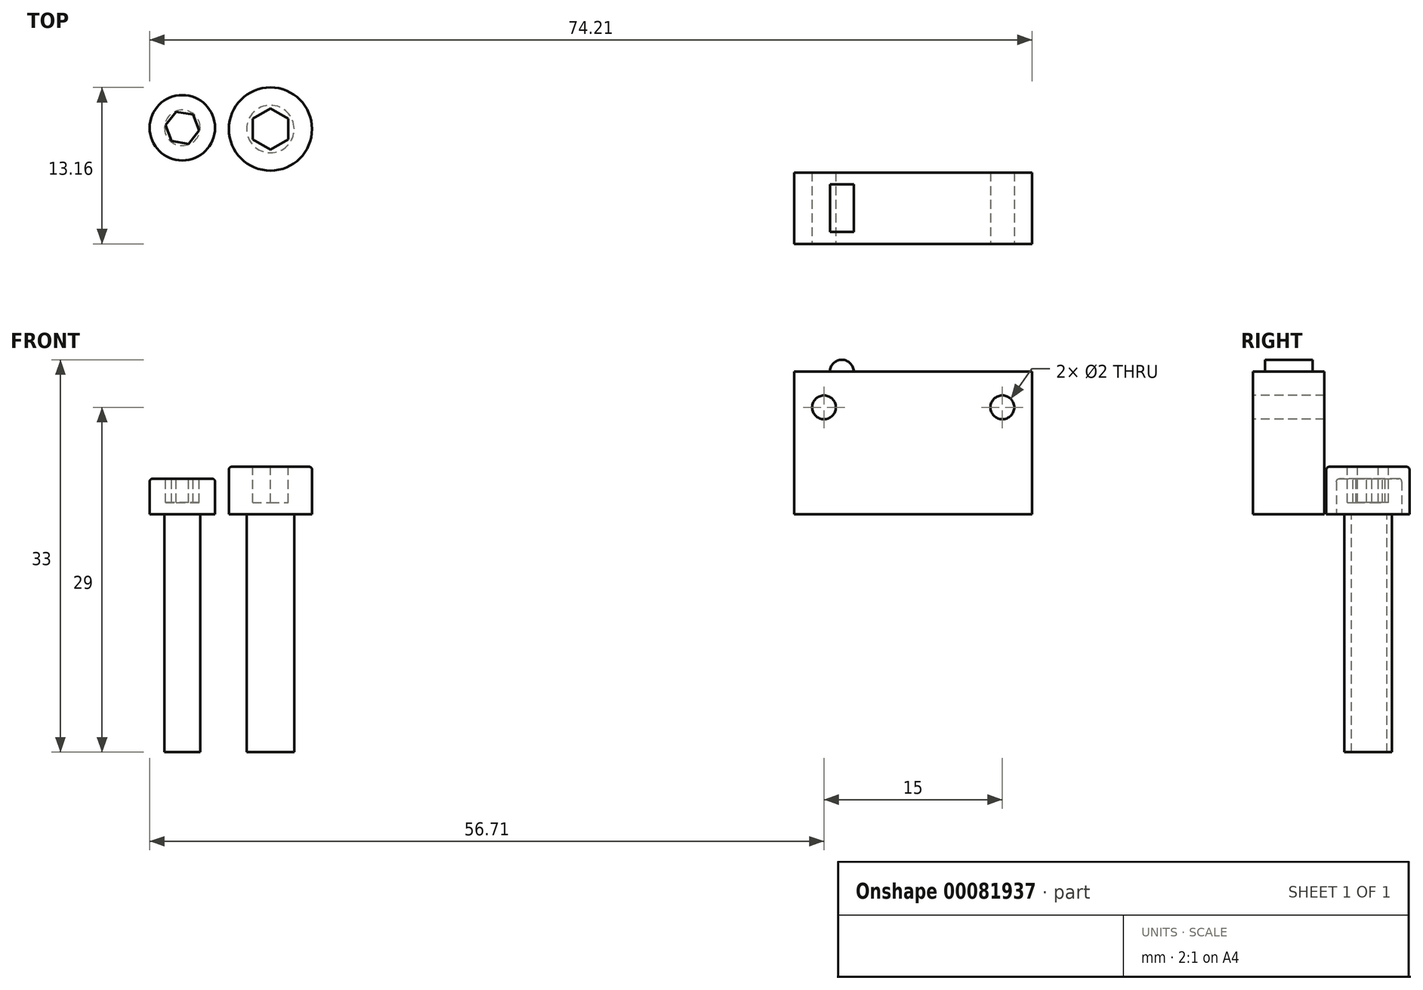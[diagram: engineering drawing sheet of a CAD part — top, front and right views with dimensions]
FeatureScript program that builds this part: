
annotation { "Feature Type Name" : "Feature", "Feature Type Description" : "" }
export const myFeature = defineFeature(function(context is Context, id is Id, definition is map)
    precondition{}
    {
        {
            var Q0;
            Q0=qCreatedBy(makeId("Front.planeOp"),FACE);
            var sketch = newSketch(context, id + "F0", { "sketchPlane" : qUnion([Q0])});
            skLineSegment(sketch, "E0.bottom", {"start": v(-10, 12) * mm, "end": v(10, 12) * mm});
            skLineSegment(sketch, "E0.top", {"start": v(-10, 0) * mm, "end": v(10, 0) * mm});
            skLineSegment(sketch, "E0.left", {"start": v(-10, 12) * mm, "end": v(-10, 0) * mm});
            skLineSegment(sketch, "E0.right", {"start": v(10, 12) * mm, "end": v(10, 0) * mm});
            skSolve(sketch);
        }
        {
            var Q0;
            Q0 = qSketchRegion(id + "F0", true);
            extrude(context, id + "F1", {"entities" : qUnion([Q0]), "endBound" : BoundingType.SYMMETRIC, "depth" : 6 * mm});
        }
        {
            var Q0;
            Q0=qCreatedBy(makeId("Front.planeOp"),FACE);
            var sketch = newSketch(context, id + "F2", { "sketchPlane" : qUnion([Q0])});
            skCircle(sketch, "E1", {"center": v(-6, 12) * mm, "radius": 1 * mm});
            skSolve(sketch);
        }
        {
            var Q0;
            Q0 = qSketchRegion(id + "F2", true);
            extrude(context, id + "F3", {"entities" : qUnion([Q0]), "operationType" : NewBodyOperationType.ADD, "endBound" : BoundingType.SYMMETRIC, "depth" : 4 * mm});
        }
        {
            var Q0;
            Q0=makeQuery(id+"F1.opExtrude","CAP_FACE",FACE,{"disambiguationData":[OSD([sQuery(id+"F0.wireOp",EDGE,"E0.bottom"),sQuery(id+"F0.wireOp",EDGE,"E0.top"),sQuery(id+"F0.wireOp",EDGE,"E0.left"),sQuery(id+"F0.wireOp",EDGE,"E0.right")])],"isStart":false});
            var sketch = newSketch(context, id + "F4", { "sketchPlane" : qUnion([Q0])});
            skCircle(sketch, "E2", {"center": v(-7.5, 9) * mm, "radius": 1 * mm});
            skCircle(sketch, "E3", {"center": v(7.5, 9) * mm, "radius": 1 * mm});
            skLineSegment(sketch, "E4", {"start": v(-7.5, 9) * mm, "end": v(7.5, 9) * mm, "construction": true});
            skLineSegment(sketch, "E5", {"start": v(0, 0) * mm, "end": v(0, 9) * mm, "construction": true});
            skSolve(sketch);
        }
        {
            var Q0;
            Q0 = qSketchRegion(id + "F4", true);
            extrude(context, id + "F5", {"entities" : qUnion([Q0]), "operationType" : NewBodyOperationType.REMOVE, "endBound" : BoundingType.THROUGH_ALL, "oppositeDirection" : true, "depth" : 25 * mm});
        }
        {
            var Q0;
            Q0=qCreatedBy(makeId("Top.planeOp"),FACE);
            var sketch = newSketch(context, id + "F6", { "sketchPlane" : qUnion([Q0])});
            skCircle(sketch, "E6", {"center": v(-61.46, 6.76) * mm, "radius": 1.5 * mm});
            skSolve(sketch);
        }
        {
            var Q0;
            Q0 = qSketchRegion(id + "F6", true);
            extrude(context, id + "F7", {"entities" : qUnion([Q0]), "oppositeDirection" : true, "depth" : 20 * mm});
        }
        {
            var Q0;
            Q0=makeQuery(id+"F7.opExtrude","CAP_FACE",FACE,{"disambiguationData":[OSD([sQuery(id+"F6.wireOp",EDGE,"E6")])],"isStart":true});
            var sketch = newSketch(context, id + "F8", { "sketchPlane" : qUnion([Q0])});
            skCircle(sketch, "E7", {"center": v(-61.46, 6.76) * mm, "radius": 2.75 * mm});
            skSolve(sketch);
        }
        {
            var Q0;
            Q0 = qSketchRegion(id + "F8", true);
            extrude(context, id + "F9", {"entities" : qUnion([Q0]), "operationType" : NewBodyOperationType.ADD, "depth" : 3 * mm});
        }
        {
            var Q0;
            Q0=makeQuery(id+"F9.opExtrude","CAP_FACE",FACE,{"disambiguationData":[OSD([sQuery(id+"F8.wireOp",EDGE,"E7")])],"isStart":false});
            var sketch = newSketch(context, id + "F10", { "sketchPlane" : qUnion([Q0])});
            skCircle(sketch, "E8.cCircle", {"center": v(-61.46, 6.76) * mm, "radius": 1.25 * mm, "construction": true});
            skLineSegment(sketch, "E8.0", {"start": v(-60.03, 6.53) * mm, "end": v(-60.94, 5.41) * mm});
            skLineSegment(sketch, "E8.1", {"start": v(-60.94, 5.41) * mm, "end": v(-62.37, 5.64) * mm});
            skLineSegment(sketch, "E8.2", {"start": v(-62.37, 5.64) * mm, "end": v(-62.88, 7) * mm});
            skLineSegment(sketch, "E8.3", {"start": v(-62.88, 7) * mm, "end": v(-61.97, 8.11) * mm});
            skLineSegment(sketch, "E8.4", {"start": v(-61.97, 8.11) * mm, "end": v(-60.55, 7.88) * mm});
            skLineSegment(sketch, "E8.5", {"start": v(-60.55, 7.88) * mm, "end": v(-60.03, 6.53) * mm});
            skPoint(sketch, "E8.0.midPoint", {"position": v(-60.49, 5.97) * mm});
            skSolve(sketch);
        }
        {
            var Q0;
            Q0 = qSketchRegion(id + "F10", true);
            extrude(context, id + "F11", {"entities" : qUnion([Q0]), "operationType" : NewBodyOperationType.REMOVE, "oppositeDirection" : true, "depth" : 2 * mm});
        }
        {
            var Q0;
            Q0=makeQuery(id+"F9.opExtrude","CAP_EDGE",EDGE,{"disambiguationData":[OSD([sQuery(id+"F8.wireOp",EDGE,"E7")])],"isStart":false});
            fillet(context, id + "F12", {"entities" : qUnion([Q0]), "radius" : .25 * mm, "tangentPropagation" : true, "allowEdgeOverflow" : false});
        }
        {
            var Q0;
            Q0=qCreatedBy(makeId("Top.planeOp"),FACE);
            var sketch = newSketch(context, id + "F13", { "sketchPlane" : qUnion([Q0])});
            skCircle(sketch, "E9", {"center": v(-54.05, 6.66) * mm, "radius": 2 * mm});
            skSolve(sketch);
        }
        {
            var Q0;
            Q0 = qSketchRegion(id + "F13", true);
            extrude(context, id + "F14", {"entities" : qUnion([Q0]), "oppositeDirection" : true, "depth" : 20 * mm});
        }
        {
            var Q0;
            Q0=makeQuery(id+"F14.opExtrude","CAP_FACE",FACE,{"disambiguationData":[OSD([sQuery(id+"F13.wireOp",EDGE,"E9")])],"isStart":true});
            var sketch = newSketch(context, id + "F15", { "sketchPlane" : qUnion([Q0])});
            skCircle(sketch, "E10", {"center": v(-54.05, 6.66) * mm, "radius": 3.5 * mm});
            skSolve(sketch);
        }
        {
            var Q0;
            Q0 = qSketchRegion(id + "F15", true);
            extrude(context, id + "F16", {"entities" : qUnion([Q0]), "operationType" : NewBodyOperationType.ADD, "depth" : 4 * mm});
        }
        {
            var Q0;
            Q0=makeQuery(id+"F16.opExtrude","CAP_FACE",FACE,{"disambiguationData":[OSD([sQuery(id+"F15.wireOp",EDGE,"E10")])],"isStart":false});
            var sketch = newSketch(context, id + "F17", { "sketchPlane" : qUnion([Q0])});
            skCircle(sketch, "E11.cCircle", {"center": v(-54.05, 6.66) * mm, "radius": 1.5 * mm, "construction": true});
            skLineSegment(sketch, "E11.0", {"start": v(-52.55, 7.52) * mm, "end": v(-52.55, 5.8) * mm});
            skLineSegment(sketch, "E11.1", {"start": v(-52.55, 5.8) * mm, "end": v(-54.05, 4.93) * mm});
            skLineSegment(sketch, "E11.2", {"start": v(-54.05, 4.93) * mm, "end": v(-55.55, 5.8) * mm});
            skLineSegment(sketch, "E11.3", {"start": v(-55.55, 5.8) * mm, "end": v(-55.55, 7.52) * mm});
            skLineSegment(sketch, "E11.4", {"start": v(-55.55, 7.52) * mm, "end": v(-54.05, 8.4) * mm});
            skLineSegment(sketch, "E11.5", {"start": v(-54.05, 8.4) * mm, "end": v(-52.55, 7.52) * mm});
            skPoint(sketch, "E11.0.midPoint", {"position": v(-52.55, 6.66) * mm});
            skSolve(sketch);
        }
        {
            var Q0;
            Q0 = qSketchRegion(id + "F17", true);
            extrude(context, id + "F18", {"entities" : qUnion([Q0]), "operationType" : NewBodyOperationType.REMOVE, "oppositeDirection" : true, "depth" : 3 * mm});
        }
        {
            var Q0;
            Q0=makeQuery(id+"F16.opExtrude","CAP_EDGE",EDGE,{"disambiguationData":[OSD([sQuery(id+"F15.wireOp",EDGE,"E10")])],"isStart":false});
            fillet(context, id + "F19", {"entities" : qUnion([Q0]), "radius" : .25 * mm, "tangentPropagation" : true, "allowEdgeOverflow" : false});
        }
    });
